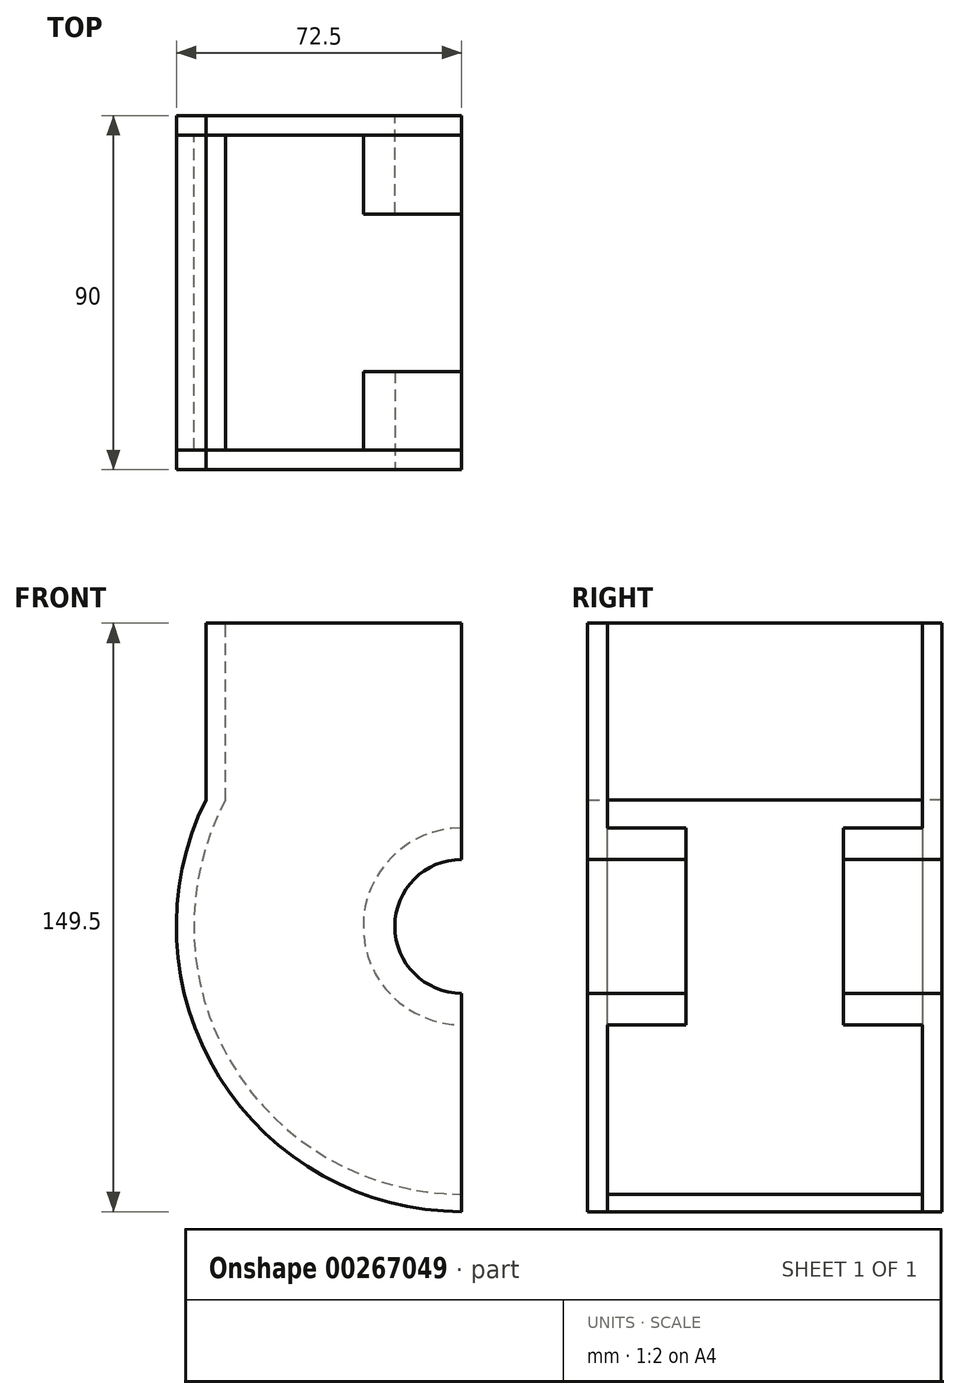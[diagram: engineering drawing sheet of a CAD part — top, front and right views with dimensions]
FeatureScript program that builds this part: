
annotation { "Feature Type Name" : "Feature", "Feature Type Description" : "" }
export const myFeature = defineFeature(function(context is Context, id is Id, definition is map)
    precondition{}
    {
        {
            var Q0;
            Q0=qCreatedBy(makeId("Front.planeOp"),FACE);
            var sketch = newSketch(context, id + "F0", { "sketchPlane" : qUnion([Q0])});
            skArc(sketch, "E0", {"start": v(0, 25) * mm, "mid": v(-25, 0) * mm, "end": v(0, -25) * mm});
            skArc(sketch, "E1", {"start": v(0, 17) * mm, "mid": v(-17, 0) * mm, "end": v(0, -17) * mm});
            skLineSegment(sketch, "E2", {"start": v(0, 25) * mm, "end": v(0, 17) * mm});
            skLineSegment(sketch, "E3.trimOffspring", {"start": v(0, -17) * mm, "end": v(0, -25) * mm});
            skSolve(sketch);
        }
        {
            var Q0;
            Q0 = qSketchRegion(id + "F0", true);
            extrude(context, id + "F1", {"entities" : qUnion([Q0]), "depth" : 20 * mm, "hasSecondDirection" : true, "secondDirectionOppositeDirection" : true, "secondDirectionDepth" : 5 * mm});
        }
        {
            var Q0;
            Q0=qCreatedBy(makeId("Front.planeOp"),FACE);
            var sketch = newSketch(context, id + "F2", { "sketchPlane" : qUnion([Q0])});
            skArc(sketch, "E4", {"start": v(-65, 32.11) * mm, "mid": v(-61.58, -38.26) * mm, "end": v(0, -72.5) * mm});
            skPoint(sketch, "E5.0", {"position": v(0, 25) * mm});
            skPoint(sketch, "E6.0", {"position": v(0, -25) * mm});
            skLineSegment(sketch, "E7", {"start": v(0, 25) * mm, "end": v(0, 77) * mm});
            skLineSegment(sketch, "E8", {"start": v(0, 77) * mm, "end": v(-65, 77) * mm});
            skLineSegment(sketch, "E9", {"start": v(-65, 77) * mm, "end": v(-65, 32.11) * mm});
            skLineSegment(sketch, "E10", {"start": v(0, -25) * mm, "end": v(0, -72.5) * mm});
            skArc(sketch, "E11", {"start": v(0, 25) * mm, "mid": v(-25, 0) * mm, "end": v(0, -25) * mm});
            skSolve(sketch);
        }
        {
            var Q0;
            Q0 = qSketchRegion(id + "F2", true);
            extrude(context, id + "F3", {"entities" : qUnion([Q0]), "operationType" : NewBodyOperationType.ADD, "oppositeDirection" : true, "depth" : 5 * mm});
        }
        {
            var Q0;
            Q0=qCreatedBy(makeId("Front.planeOp"),FACE);
            cPlane(context, id + "F4", {"entities" : qUnion([Q0]), "cplaneType" : CPlaneType.OFFSET, "offset" : 40 * mm, "width" : 150 * mm, "height" : 150 * mm});
        }
        {
            var Q0;
            Q0=makeQuery(id+"F1.opExtrude","SWEPT_BODY",BODY,{"disambiguationData":[OSD([sQuery(id+"F0.wireOp",EDGE,"E0"),sQuery(id+"F0.wireOp",EDGE,"E1"),sQuery(id+"F0.wireOp",EDGE,"E2"),sQuery(id+"F0.wireOp",EDGE,"E3.trimOffspring")])]});
            var Q1;
            Q1=qCreatedBy(id+"F4.planeOp",FACE);
            mirror(context, id + "F5", {"entities" : qUnion([Q0]), "mirrorPlane" : qUnion([Q1])});
        }
        {
            var Q0;
            Q0=makeQuery(id+"F3.opExtrude","CAP_FACE",FACE,{"disambiguationData":[OSD([sQuery(id+"F2.wireOp",EDGE,"E4"),sQuery(id+"F2.wireOp",EDGE,"E7"),sQuery(id+"F2.wireOp",EDGE,"E8"),sQuery(id+"F2.wireOp",EDGE,"E9"),sQuery(id+"F2.wireOp",EDGE,"E10"),sQuery(id+"F2.wireOp",EDGE,"E11")])],"isStart":true});
            var sketch = newSketch(context, id + "F6", { "sketchPlane" : qUnion([Q0])});
            skArc(sketch, "E12.0", {"start": v(-65, 32.11) * mm, "mid": v(-61.58, -38.26) * mm, "end": v(0, -72.5) * mm});
            skLineSegment(sketch, "E13.0", {"start": v(-65, 77) * mm, "end": v(-65, 32.11) * mm});
            skLineSegment(sketch, "E14.0", {"start": v(-60, 77) * mm, "end": v(-65, 77) * mm});
            skLineSegment(sketch, "E15", {"start": v(-60, 77) * mm, "end": v(-60, 32.11) * mm});
            skArc(sketch, "E16", {"start": v(-60, 32.11) * mm, "mid": v(-58.38, -34.97) * mm, "end": v(0, -68.05) * mm});
            skLineSegment(sketch, "E17", {"start": v(0, -72.5) * mm, "end": v(0, -68.05) * mm});
            skPoint(sketch, "E18.orphan", {"position": v(0, 77) * mm});
            skSolve(sketch);
        }
        {
            var Q0;
            Q0 = qSketchRegion(id + "F6", true);
            var Q1;
            Q1=makeQuery(id+"F5.opPattern","COPY",FACE,{"derivedFrom":makeQuery(id+"F3.opExtrude","CAP_FACE",FACE,{"disambiguationData":[OSD([sQuery(id+"F2.wireOp",EDGE,"E4"),sQuery(id+"F2.wireOp",EDGE,"E7"),sQuery(id+"F2.wireOp",EDGE,"E8"),sQuery(id+"F2.wireOp",EDGE,"E9"),sQuery(id+"F2.wireOp",EDGE,"E10"),sQuery(id+"F2.wireOp",EDGE,"E11")])],"isStart":true}),"instanceName":"1"});
            extrude(context, id + "F7", {"entities" : qUnion([Q0]), "endBound" : BoundingType.UP_TO_SURFACE, "endBoundEntityFace" : qUnion([Q1]), "depth" : 25 * mm});
        }
    });
